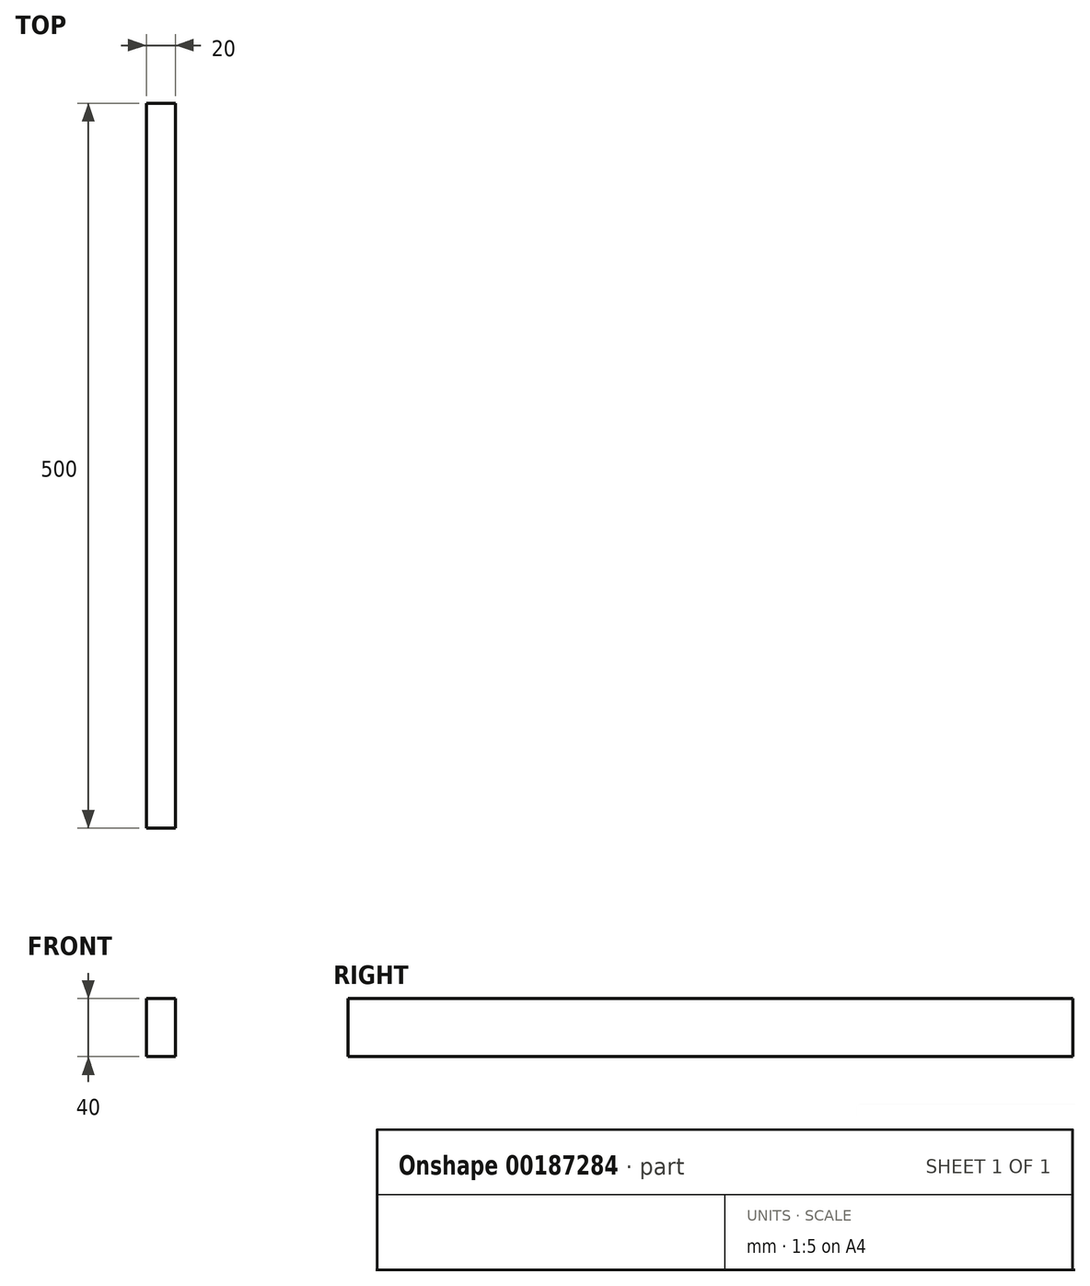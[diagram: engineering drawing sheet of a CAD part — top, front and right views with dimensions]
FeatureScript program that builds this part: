
annotation { "Feature Type Name" : "Feature", "Feature Type Description" : "" }
export const myFeature = defineFeature(function(context is Context, id is Id, definition is map)
    precondition{}
    {
        {
            var Q0;
            Q0=qCreatedBy(makeId("Front.planeOp"),FACE);
            var sketch = newSketch(context, id + "F0", { "sketchPlane" : qUnion([Q0])});
            skLineSegment(sketch, "E0.bottom", {"start": v(-10, 20) * mm, "end": v(10, 20) * mm});
            skLineSegment(sketch, "E0.top", {"start": v(-10, -20) * mm, "end": v(10, -20) * mm});
            skLineSegment(sketch, "E0.left", {"start": v(-10, 20) * mm, "end": v(-10, -20) * mm});
            skLineSegment(sketch, "E0.right", {"start": v(10, 20) * mm, "end": v(10, -20) * mm});
            skPoint(sketch, "E1", {"position": v(0, 20) * mm});
            skPoint(sketch, "E2", {"position": v(10, 0) * mm});
            skSolve(sketch);
        }
        {
            var Q0;
            Q0=makeQuery(id+"F0.imprint","IMPRINT",FACE,{"disambiguationData":[TD([[makeQuery(id+"F0.imprint","IMPRINT",EDGE,{"derivedFrom":sQuery(id+"F0.wireOp",EDGE,"E0.bottom")}),-1.0]])]});
            extrude(context, id + "F1", {"entities" : qUnion([Q0]), "depth" : 500 * mm});
        }
    });
